# Revit family: Pot_Filler-Kitchen-Grohe-Ladylux-31075_Series
name_source: partatom
category: Plumbing Fixtures
revit_build: Autodesk Revit 2014 (Build: 20130308_1515(x64)
units: mm (PartAtom-declared; Revit-internal decimal feet)

## types (1)
- 31075DC2
    ADA Compliant = Yes
    Assembly Code = D2020300
    CW Connection = Yes
    CWFU = 1.5
    CalGreen Compliant = Yes
    Cold Water Connection Diameter = 1/2"
    Cold Water Connection Radius = 1/4"
    Default Elevation = 0"
    Description = Ladylux Wallmount Pot Filler
    Finish = Brass-Grohe-DC2-SuperSteel
    Flow Rate = 1.75 gpm (6.6 L/min.)
    HW Connection = Yes
    HWFU = 1.5
    Height = 3 25/32"
    Installation Type = Wall Mounted
    Length = 24 13/32"
    Manufacturer = Grohe
    Material = Brass-Grohe-DC2-SuperSteel
    Model = 31075DC2
    Price = Prices may vary. Please consult Manufacturer Representative for most up-to-date price list.
    Shipping Weight = 5.610 lb
    URL = https://www.grohe.us
    Vent Connection = No
    WFU = 2
    Warranty Documentation Link = https://cdn.cloud.grohe.com
    Waste Connection = No
    Width = 2 3/8"
    cUPC Compliant = Yes

## geometry (parser evidence)
native form markers: Sweep x3
no freeform markers — native parametric forms only
